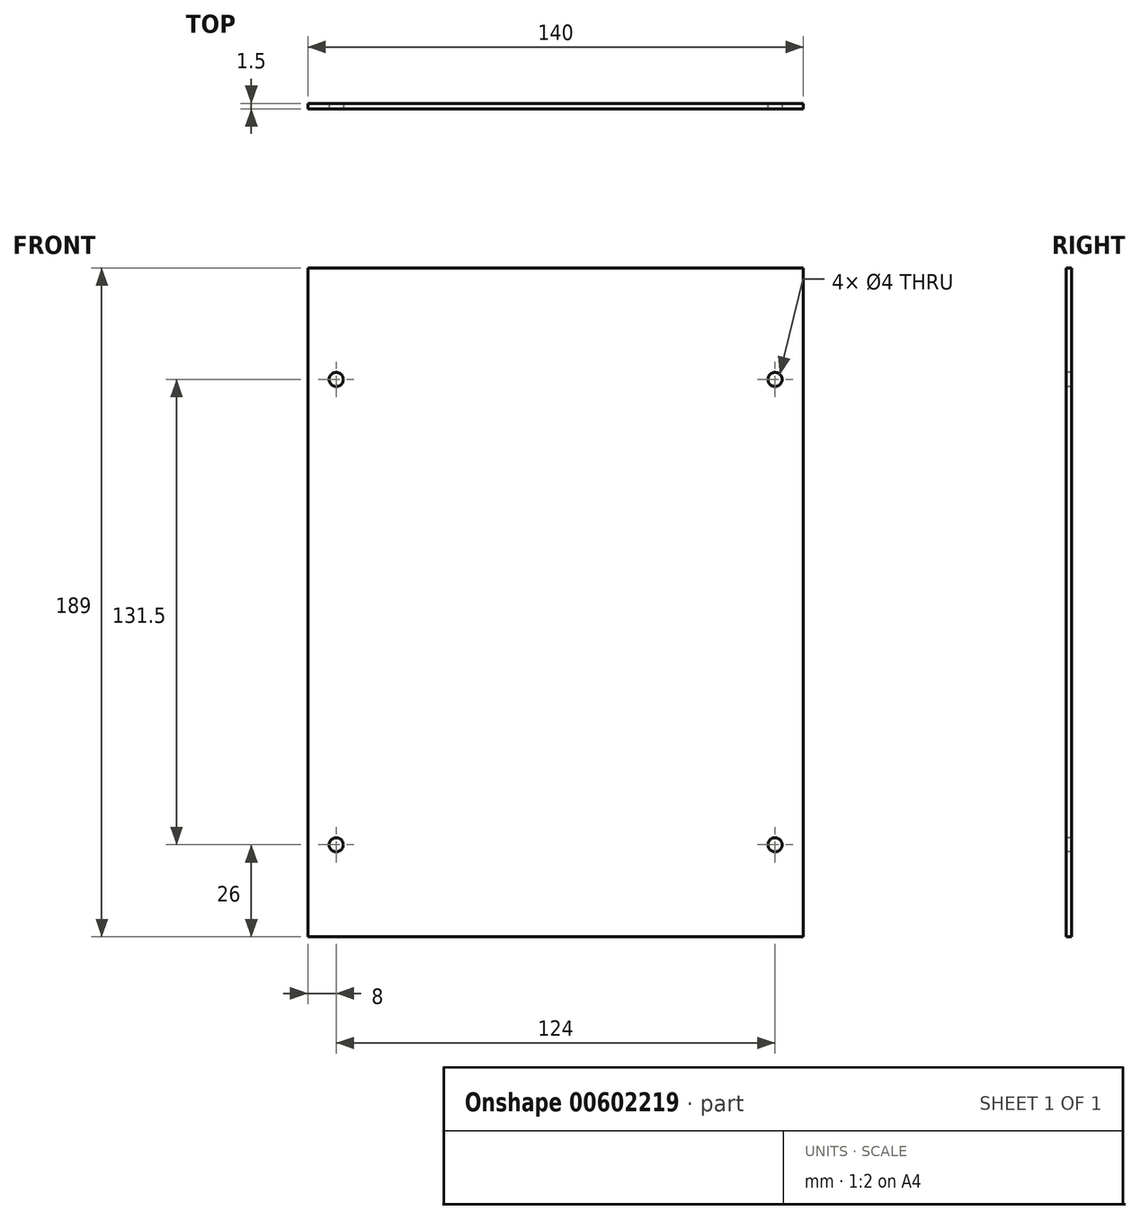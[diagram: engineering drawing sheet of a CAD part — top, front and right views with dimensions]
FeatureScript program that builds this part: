
annotation { "Feature Type Name" : "Feature", "Feature Type Description" : "" }
export const myFeature = defineFeature(function(context is Context, id is Id, definition is map)
    precondition{}
    {
        {
            var Q0;
            Q0=qCreatedBy(makeId("Front.planeOp"),FACE);
            var sketch = newSketch(context, id + "F0", { "sketchPlane" : qUnion([Q0])});
            skLineSegment(sketch, "E0.bottom", {"start": v(70, -94.5) * mm, "end": v(-70, -94.5) * mm});
            skLineSegment(sketch, "E0.top", {"start": v(70, 94.5) * mm, "end": v(-70, 94.5) * mm});
            skLineSegment(sketch, "E0.left", {"start": v(70, -94.5) * mm, "end": v(70, 94.5) * mm});
            skLineSegment(sketch, "E0.right", {"start": v(-70, -94.5) * mm, "end": v(-70, 94.5) * mm});
            skPoint(sketch, "E0.middle", {"position": v(0, 0) * mm});
            skSolve(sketch);
        }
        {
            var Q0;
            Q0=makeQuery(id+"F0.imprint","IMPRINT",FACE,{"disambiguationData":[TD([[makeQuery(id+"F0.imprint","IMPRINT",EDGE,{"derivedFrom":sQuery(id+"F0.wireOp",EDGE,"E0.bottom")}),-1.0]])]});
            extrude(context, id + "F1", {"entities" : qUnion([Q0]), "depth" : 1.5 * mm, "offsetDistance" : 25 * mm});
        }
        {
            var Q0;
            Q0=makeQuery(id+"F1.opExtrude","CAP_FACE",FACE,{"disambiguationData":[OSD([sQuery(id+"F0.wireOp",EDGE,"E0.bottom"),sQuery(id+"F0.wireOp",EDGE,"E0.top"),sQuery(id+"F0.wireOp",EDGE,"E0.left"),sQuery(id+"F0.wireOp",EDGE,"E0.right")])],"isStart":false});
            var sketch = newSketch(context, id + "F2", { "sketchPlane" : qUnion([Q0])});
            skPoint(sketch, "E1", {"position": v(62, 63) * mm});
            skPoint(sketch, "E2", {"position": v(62, -68.5) * mm});
            skPoint(sketch, "E3.MirrorP", {"position": v(-62, 63) * mm});
            skPoint(sketch, "E4.MirrorP", {"position": v(-62, -68.5) * mm});
            skSolve(sketch);
        }
        {
            var Q0;
            Q0=sQuery(id+"F2.wireOp",VERTEX,"E3.MirrorP");
            var Q1;
            Q1=sQuery(id+"F2.wireOp",VERTEX,"E1");
            var Q2;
            Q2=sQuery(id+"F2.wireOp",VERTEX,"E2");
            var Q3;
            Q3=sQuery(id+"F2.wireOp",VERTEX,"E4.MirrorP");
            var Q4;
            Q4=makeQuery(id+"F1.opExtrude","SWEPT_BODY",BODY,{"disambiguationData":[OSD([sQuery(id+"F0.wireOp",EDGE,"E0.bottom"),sQuery(id+"F0.wireOp",EDGE,"E0.top"),sQuery(id+"F0.wireOp",EDGE,"E0.left"),sQuery(id+"F0.wireOp",EDGE,"E0.right")])]});
            hole(context, id + "F3", {"style" : HoleStyle.SIMPLE, "endStyle" : HoleEndStyle.THROUGH, "standardTappedOrClearance" : lookupTablePath({ "standard" : "ISO", "size" : "4", "type" : "Drilled" }), "standardBlindInLast" : lookupTablePath({ "standard" : "ISO", "size" : "4", "type" : "Drilled" }), "holeDiameter" : 4 * mm, "majorDiameter" : 5 * mm, "isTappedThrough" : true, "tappedDepth" : 12 * mm, "tapClearance" : 3, "locations" : qUnion([Q0, Q1, Q2, Q3]), "scope" : qUnion([Q4])});
        }
    });
